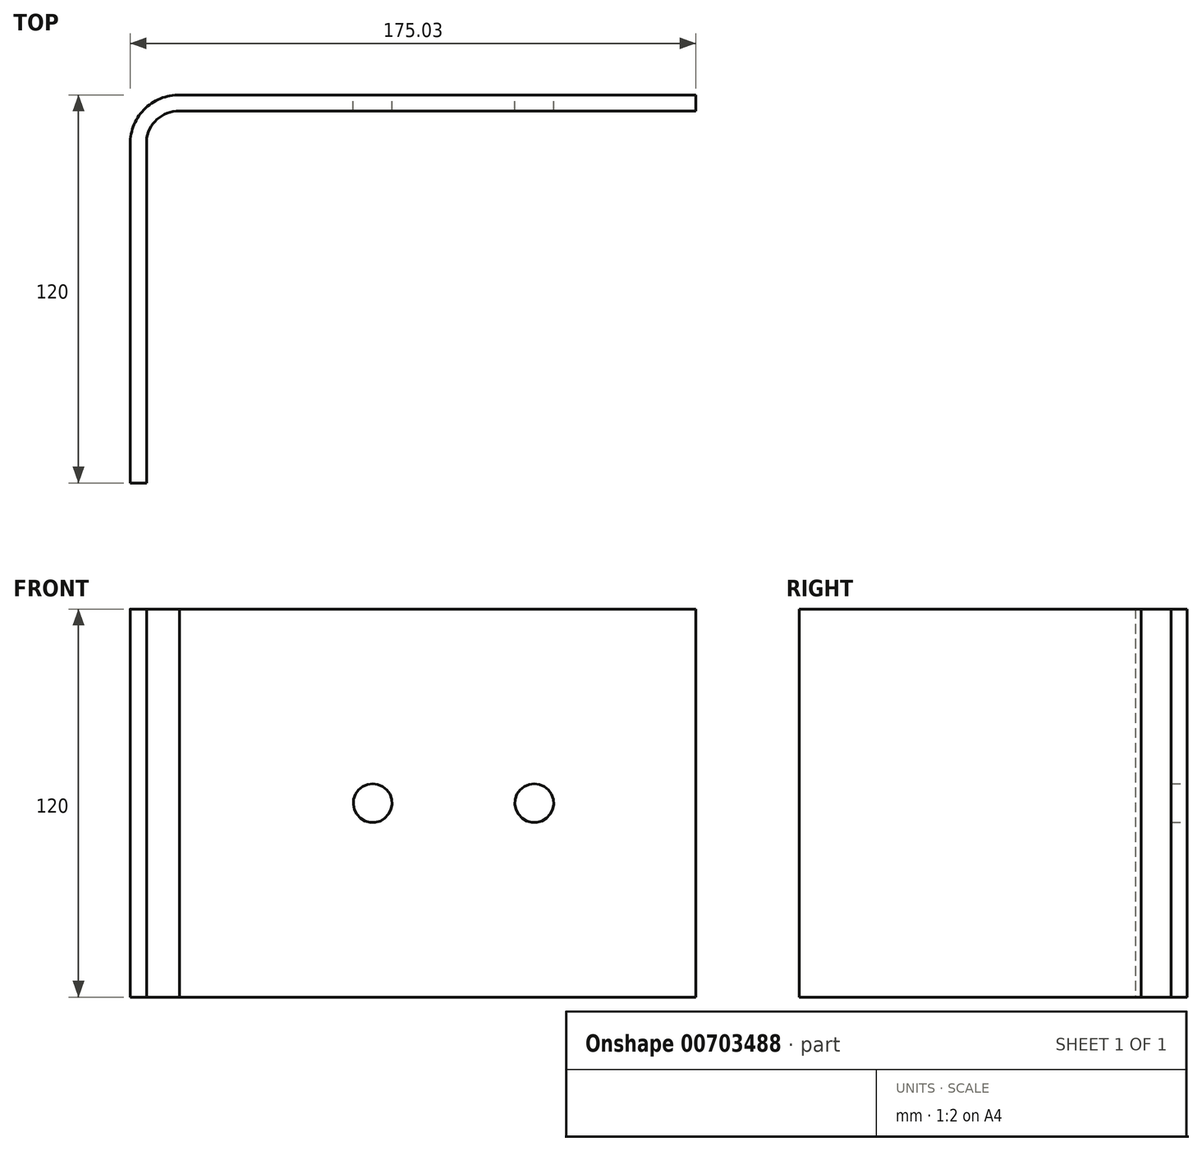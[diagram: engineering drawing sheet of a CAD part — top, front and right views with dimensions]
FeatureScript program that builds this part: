
annotation { "Feature Type Name" : "Feature", "Feature Type Description" : "" }
export const myFeature = defineFeature(function(context is Context, id is Id, definition is map)
    precondition{}
    {
        {
            var Q0;
            Q0=qCreatedBy(makeId("Top.planeOp"),FACE);
            var sketch = newSketch(context, id + "F0", { "sketchPlane" : qUnion([Q0])});
            skArc(sketch, "E0", {"start": v(-28.38, 31.77) * mm, "mid": v(-28.38, 31.77) * mm, "end": v(-28.38, 31.77) * mm});
            skLineSegment(sketch, "E1", {"start": v(-39.18, 36.77) * mm, "end": v(120.46, 36.77) * mm});
            skLineSegment(sketch, "E2", {"start": v(-54.54, 20.82) * mm, "end": v(-54.54, -83.23) * mm});
            skArc(sketch, "E3.0", {"start": v(-39.34, 31.77) * mm, "mid": v(-46.28, 29.18) * mm, "end": v(-49.54, 22.53) * mm});
            skLineSegment(sketch, "E4", {"start": v(-49.54, 22.53) * mm, "end": v(-49.54, -83.23) * mm});
            skLineSegment(sketch, "E5", {"start": v(-49.54, -83.23) * mm, "end": v(-54.54, -83.23) * mm});
            skLineSegment(sketch, "E6", {"start": v(-39.34, 31.77) * mm, "end": v(120.46, 31.77) * mm});
            skLineSegment(sketch, "E7", {"start": v(120.46, 31.77) * mm, "end": v(120.46, 36.77) * mm});
            skArc(sketch, "E8.trimOffspring", {"start": v(-49.54, 10.56) * mm, "mid": v(-49.54, 10.56) * mm, "end": v(-49.54, 10.56) * mm});
            skArc(sketch, "E9.trimOffspring", {"start": v(-39.18, 36.77) * mm, "mid": v(-50.37, 32.17) * mm, "end": v(-54.54, 20.82) * mm});
            skSolve(sketch);
        }
        {
            var Q0;
            Q0=qSketchRegion(id+"F0",true);
            extrude(context, id + "F1", {"entities" : qUnion([Q0]), "depth" : 120 * mm, "offsetDistance" : 25 * mm});
        }
        {
            var Q0;
            Q0=makeQuery(id+"F1.opExtrude","SWEPT_FACE",FACE,{"disambiguationData":[OSD([sQuery(id+"F0.wireOp",EDGE,"E1")])]});
            var sketch = newSketch(context, id + "F2", { "sketchPlane" : qUnion([Q0])});
            skCircle(sketch, "E10", {"center": v(-70.46, 60) * mm, "radius": 6 * mm});
            skCircle(sketch, "E11", {"center": v(-20.46, 60) * mm, "radius": 6 * mm});
            skSolve(sketch);
        }
        {
            var Q0;
            Q0=makeQuery(id+"F2.imprint","IMPRINT",FACE,{"disambiguationData":[TD([[makeQuery(id+"F2.imprint","IMPRINT",EDGE,{"derivedFrom":sQuery(id+"F2.wireOp",EDGE,"E10")}),1.0]])]});
            var Q1;
            Q1=makeQuery(id+"F2.imprint","IMPRINT",FACE,{"disambiguationData":[TD([[makeQuery(id+"F2.imprint","IMPRINT",EDGE,{"derivedFrom":sQuery(id+"F2.wireOp",EDGE,"E11")}),1.0]])]});
            var Q2;
            Q2=sQuery(id+"F2.wireOp",EDGE,"E11");
            var Q3;
            Q3=sQuery(id+"F2.wireOp",EDGE,"E10");
            extrude(context, id + "F3", {"entities" : qUnion([Q0, Q1]), "operationType" : NewBodyOperationType.REMOVE, "surfaceEntities" : qUnion([Q2, Q3]), "oppositeDirection" : true, "depth" : 5 * mm, "offsetDistance" : 25 * mm});
        }
        {
            var Q0;
            Q0=makeQuery(id+"F1.opExtrude","SWEPT_FACE",FACE,{"disambiguationData":[OSD([sQuery(id+"F0.wireOp",EDGE,"E4")])]});
            var sketch = newSketch(context, id + "F4", { "sketchPlane" : qUnion([Q0])});
            skLineSegment(sketch, "E12", {"start": v(-7.47, 160.68) * mm, "end": v(-347.47, 160.68) * mm});
            skLineSegment(sketch, "E13", {"start": v(-377.47, 190.68) * mm, "end": v(-377.47, 240.68) * mm});
            skLineSegment(sketch, "E14", {"start": v(-357.47, 260.68) * mm, "end": v(-147.47, 260.68) * mm});
            skLineSegment(sketch, "E15", {"start": v(-127.47, 280.68) * mm, "end": v(-127.47, 380.68) * mm});
            skLineSegment(sketch, "E16", {"start": v(-97.47, 410.68) * mm, "end": v(-7.47, 410.68) * mm});
            skLineSegment(sketch, "E17", {"start": v(22.53, 380.68) * mm, "end": v(22.53, 190.68) * mm});
            skPoint(sketch, "E18.visualSharp", {"position": v(-127.47, 410.68) * mm});
            skArc(sketch, "E18.filletArc", {"start": v(-97.47, 410.68) * mm, "mid": v(-118.68, 401.9) * mm, "end": v(-127.47, 380.68) * mm});
            skPoint(sketch, "E19.visualSharp", {"position": v(22.53, 410.68) * mm});
            skArc(sketch, "E19.filletArc", {"start": v(22.53, 380.68) * mm, "mid": v(13.74, 401.9) * mm, "end": v(-7.47, 410.68) * mm});
            skPoint(sketch, "E20.visualSharp", {"position": v(22.53, 160.68) * mm});
            skArc(sketch, "E20.filletArc", {"start": v(-7.47, 160.68) * mm, "mid": v(13.74, 169.47) * mm, "end": v(22.53, 190.68) * mm});
            skPoint(sketch, "E21.visualSharp", {"position": v(-377.47, 160.68) * mm});
            skArc(sketch, "E21.filletArc", {"start": v(-377.47, 190.68) * mm, "mid": v(-368.68, 169.47) * mm, "end": v(-347.47, 160.68) * mm});
            skPoint(sketch, "E22.visualSharp", {"position": v(-377.47, 260.68) * mm});
            skArc(sketch, "E22.filletArc", {"start": v(-357.47, 260.68) * mm, "mid": v(-371.61, 254.82) * mm, "end": v(-377.47, 240.68) * mm});
            skPoint(sketch, "E23.visualSharp", {"position": v(-127.47, 260.68) * mm});
            skArc(sketch, "E23.filletArc", {"start": v(-147.47, 260.68) * mm, "mid": v(-133.33, 266.54) * mm, "end": v(-127.47, 280.68) * mm});
            skCircle(sketch, "E24", {"center": v(-87.47, 360.68) * mm, "radius": 6 * mm});
            skCircle(sketch, "E25", {"center": v(-7.47, 360.68) * mm, "radius": 6 * mm});
            skSolve(sketch);
        }
        {
            var Q0;
            Q0 = qSketchRegion(id + "F4", true);
            extrude(context, id + "F5", {"entities" : qUnion([Q0]), "depth" : 5 * mm, "offsetDistance" : 25 * mm});
        }
        {
            var Q0;
            Q0=makeQuery(id+"F5.opExtrude","SWEPT_BODY",BODY,{"disambiguationData":[OSD([sQuery(id+"F4.wireOp",EDGE,"E12"),sQuery(id+"F4.wireOp",EDGE,"E13"),sQuery(id+"F4.wireOp",EDGE,"E14"),sQuery(id+"F4.wireOp",EDGE,"E15"),sQuery(id+"F4.wireOp",EDGE,"E16"),sQuery(id+"F4.wireOp",EDGE,"E17"),sQuery(id+"F4.wireOp",EDGE,"E18.filletArc"),sQuery(id+"F4.wireOp",EDGE,"E19.filletArc"),sQuery(id+"F4.wireOp",EDGE,"E20.filletArc"),sQuery(id+"F4.wireOp",EDGE,"E21.filletArc"),sQuery(id+"F4.wireOp",EDGE,"E22.filletArc"),sQuery(id+"F4.wireOp",EDGE,"E23.filletArc"),sQuery(id+"F4.wireOp",EDGE,"E24"),sQuery(id+"F4.wireOp",EDGE,"E25")])]});
            deleteBodies(context, id + "F6", {"entities" : qUnion([Q0])});
        }
    });
